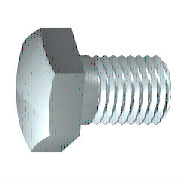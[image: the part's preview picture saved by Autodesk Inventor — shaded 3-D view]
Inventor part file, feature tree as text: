
AUTODESK INVENTOR PART (.ipt)
format: ipt  version: 2023 (Build 270158000, 158)  size: 194,560 bytes
history: native  units: mm (DEFAULTED — no unit token found)
features: sketch x3, other x2, extrude x1, plane x1
ambient origin geometry x7: Origin, YZ Plane, XZ Plane, X Axis, Y Axis, Z Axis, Center Point
bodies: Solid1 (feature_tree)
feature tree (7):
  other  "Corpo"
  extrude  "Testa"  Depth=70.0mm
  other  "Smusso1"
  plane  "Work Plane1"
  sketch  "Schizzo1"
  sketch  "Schizzo2"
  sketch  "Schizzo4"
